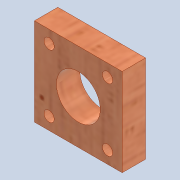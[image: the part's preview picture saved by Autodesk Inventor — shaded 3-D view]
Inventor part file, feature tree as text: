
AUTODESK INVENTOR PART (.ipt)
format: ipt  version: 2020 (Build 240168000, 168)  size: 240,128 bytes
history: native  units: mm
features: extrude x3, sketch x3
ambient origin geometry x8: Origin, YZ Plane, XZ Plane, XY Plane, X Axis, Y Axis, Z Axis, Center Point
bodies: Solid1 (feature_tree)
feature tree (6):
  extrude  "Extrusion1"  Depth=30.0mm
  extrude  "Extrusion2"  TaperAngle=0.0deg  [1 undecoded]
  extrude  "Extrusion3"  TaperAngle=0.0deg  [1 undecoded]
  sketch  "Sketch1"  dims[d0=30.0mm d1=30.0mm]
  sketch  "Sketch2"  dims[d2=8.0mm d3=0.0mm d6=0.0mm d7=0.0mm]
  sketch  "Sketch3"  dims[d9=3.5mm d15=0.0mm d16=0.0mm d17=15.0mm d19=10.75mm d20=10.75mm d21=20.0mm d22=21.5mm]
note: 2 required parameter values undecoded (feature->parameter linkage not recoverable at this tier; creation-order binding heuristic only, values carry confidence <= 0.55)
